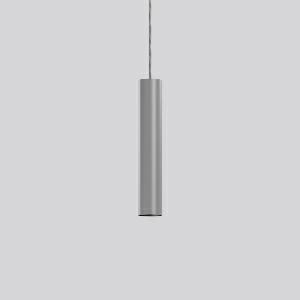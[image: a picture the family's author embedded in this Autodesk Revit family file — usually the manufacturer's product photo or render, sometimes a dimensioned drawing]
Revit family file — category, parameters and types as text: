
# Revit family: deecos_p_micro_911492_004_76_c1f5
name_source: partatom
category: Lighting Fixtures
units: mm (PartAtom-declared; Revit-internal decimal feet)

## family parameters
Cut with Voids When Loaded = No
Host = Face
Light Source = No
Part Type = Normal
Room Calculation Point = No
Round Connector Dimension = Use Diameter
Shared = No

## types (1)
- DEECOS P micro (1 x LED Modul 927, 1150 lm, 2700)
    Apparent Load = 16 VA
    CIE Flux Codes = 92 99 100 100 100
    Color Rendering = 92
    Color Temperature = 2700
    Default Elevation = 1800 mm
    Description = Series: DEECOS P micro
Cylindrical pendant luminaire. Housing: die-cast aluminium, powder-coated. Canopy made of powder-coated sheet steel with magnetic attachment. Optical assembly with lens made of plastic (polycarbonate) for the best homogeneous light distribution - can be changed without tools. Black plastic ring and recessed LED to prevent glare from the side. Best colour rendering index Ra>90. Transparent suspension cable 3 m, can be shortened. High quality converter without flickering and stroboscopic effect. 
Colour: silver
Diameter: 60 mm
Height: 340 mm
Suspension length: 3000 mm
Lamp: LED
Socket: without socket
Colour temperature: 2700K
Colour rendering index (CRI): 92
System power: 16 W
Rated luminous flux: 1150 lm
Luminous efficiency: 72 lm/W
Control gear: Converter, dimmable, DALI
Protection class: I
Type of protection: IP 20
    Height = 340 mm
    Lamp = 1 x LED Modul 927
    Lamp Light Flux = 1150 lm
    Lamp count = 1
    Length = 60 mm  [stored 0.19685 ft]
    Lifetime = 50000 h
    Luminous efficacy = 72 lm/W
    Manufacturer = RZB
    ModVariant = No
    Model = 911492.004.76
    Mounting Place = Ceiling
    Mounting Type = Pendant
    Number of Poles = 1
    OnlyDefault = Yes
    Power Factor = 1
    Product Name = DEECOS P micro
    Product group = Pendant luminaires
    ProductGroupID = 902
    Protection Class = Protection class I
    Protection Degree = Degree of protection
    RLX_Detail_Level = 1
    RLX_Emergency_Light_Flux = 0 lm
    RLX_Emergency_Type = 0
    RLX_Emergency_Type_DB = No
    RlxData = <blob elided: 31321 chars, md5=46047cff>
    Socket = socket
    Standby Power = 0 W
    System Light Flux = 1150 lm
    System Power = 16 W
    Type Comments = Product without accessories
    Type Image = 911491.004.jpg
    URL = http://relux.com
    VarID = ---
    Voltage = 0 V
    Weight = 0.00 kg
    Width = 0 mm  [stored 0 ft]

note: [stored X ft] marks values corroborated as IEEE doubles in the binary element streams (Revit-internal decimal feet)

## geometry (parser evidence)
native form markers: Blend x4, Sweep x12
no freeform markers — native parametric forms only
